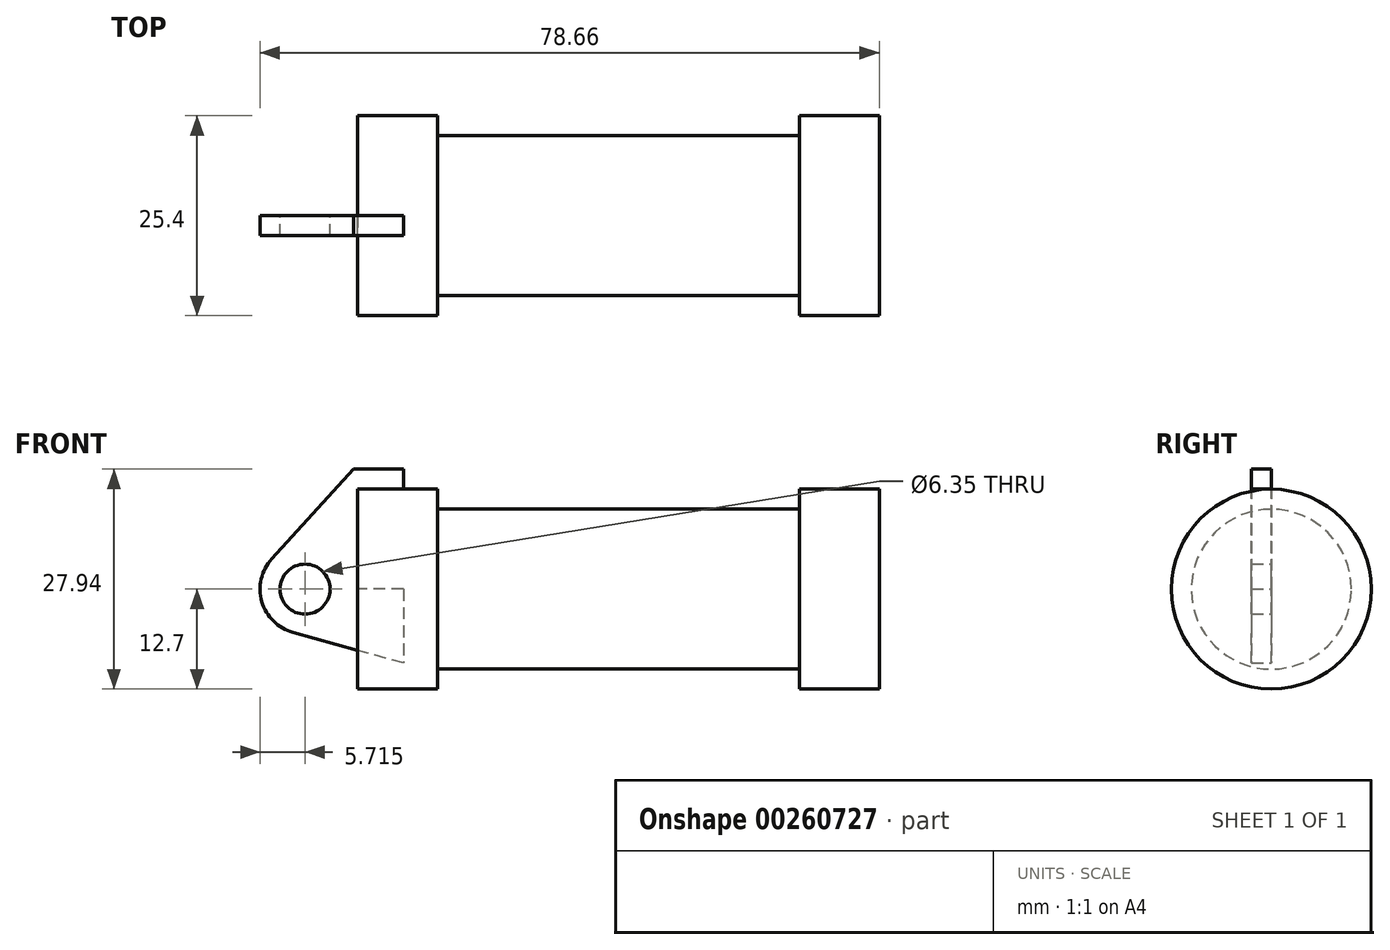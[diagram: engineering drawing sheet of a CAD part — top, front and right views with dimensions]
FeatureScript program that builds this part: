
annotation { "Feature Type Name" : "Feature", "Feature Type Description" : "" }
export const myFeature = defineFeature(function(context is Context, id is Id, definition is map)
    precondition{}
    {
        {
            var Q0;
            Q0=qCreatedBy(makeId("Front.planeOp"),FACE);
            var sketch = newSketch(context, id + "F0", { "sketchPlane" : qUnion([Q0])});
            skLineSegment(sketch, "E0", {"start": v(0, 0) * mm, "end": v(0, 12.7) * mm});
            skLineSegment(sketch, "E1", {"start": v(0, 12.7) * mm, "end": v(10.16, 12.7) * mm});
            skLineSegment(sketch, "E2", {"start": v(10.16, 12.7) * mm, "end": v(10.16, 10.16) * mm});
            skLineSegment(sketch, "E3", {"start": v(10.16, 10.16) * mm, "end": v(56.13, 10.16) * mm});
            skLineSegment(sketch, "E4", {"start": v(56.13, 10.16) * mm, "end": v(56.13, 12.7) * mm});
            skLineSegment(sketch, "E5", {"start": v(56.13, 12.7) * mm, "end": v(66.3, 12.7) * mm});
            skLineSegment(sketch, "E6", {"start": v(66.3, 12.7) * mm, "end": v(66.3, 0) * mm});
            skLineSegment(sketch, "E7", {"start": v(66.3, 0) * mm, "end": v(0, 0) * mm});
            skLineSegment(sketch, "E8", {"start": v(5.84, 15.24) * mm, "end": v(-0.5, 15.24) * mm});
            skLineSegment(sketch, "E9", {"start": v(-0.5, 15.24) * mm, "end": v(-10.88, 3.85) * mm});
            skLineSegment(sketch, "E10", {"start": v(0, 0) * mm, "end": v(-6.65, 0) * mm});
            skCircle(sketch, "E11", {"center": v(-6.65, 0) * mm, "radius": 5.72 * mm});
            skCircle(sketch, "E12", {"center": v(-6.65, 0) * mm, "radius": 3.18 * mm});
            skLineSegment(sketch, "E13", {"start": v(5.84, 15.24) * mm, "end": v(5.84, -9.4) * mm});
            skLineSegment(sketch, "E14", {"start": v(5.84, -9.4) * mm, "end": v(-8.18, -5.5) * mm});
            skLineSegment(sketch, "E15", {"start": v(5.84, 0) * mm, "end": v(5.84, 12.7) * mm});
            skLineSegment(sketch, "E16", {"start": v(5.84, 12.7) * mm, "end": v(5.84, 0) * mm});
            skLineSegment(sketch, "E17", {"start": v(5.84, 0) * mm, "end": v(66.3, 0) * mm});
            skSolve(sketch);
        }
        {
            var Q0;
            {var subQ0=sQuery(id+"F0.wireOp",EDGE,"E2");Q0=makeQuery(id+"F0.imprint","IMPRINT",FACE,{"disambiguationData":[TD([[makeQuery(id+"F0.imprint","IMPRINT",EDGE,{"derivedFrom":subQ0}),-1.0]])]});}
            var Q1;
            {var subQ0=sQuery(id+"F0.wireOp",EDGE,"E0");Q1=makeQuery(id+"F0.imprint","IMPRINT",FACE,{"disambiguationData":[TD([[makeQuery(id+"F0.imprint","IMPRINT",EDGE,{"derivedFrom":subQ0}),-1.0]])]});}
            var Q2;
            Q2=sQuery(id+"F0.wireOp",EDGE,"E7");
            revolve(context, id + "F1", {"entities" : qUnion([Q0, Q1]), "axis" : qUnion([Q2]), "revolveType" : RevolveType.FULL});
        }
        {
            var Q0;
            {var subQ4=sQuery(id+"F0.wireOp",EDGE,"E12");Q0=makeQuery(id+"F0.imprint","IMPRINT",FACE,{"disambiguationData":[TD([[makeQuery(id+"F0.imprint","IMPRINT",EDGE,{"derivedFrom":subQ4}),-1.0]])]});}
            var Q1;
            {var subQ1=sQuery(id+"F0.wireOp",EDGE,"E7");Q1=makeQuery(id+"F0.imprint","IMPRINT",FACE,{"disambiguationData":[TD([[makeQuery(id+"F0.imprint","IMPRINT",EDGE,{"derivedFrom":subQ1}),1.0]])]});}
            var Q2;
            {var subQ3=sQuery(id+"F0.wireOp",EDGE,"E0");Q2=makeQuery(id+"F0.imprint","IMPRINT",FACE,{"disambiguationData":[TD([[makeQuery(id+"F0.imprint","IMPRINT",EDGE,{"derivedFrom":subQ3}),1.0]])]});}
            extrude(context, id + "F2", {"entities" : qUnion([Q0, Q1, Q2]), "depth" : 2.54 * mm});
        }
    });
